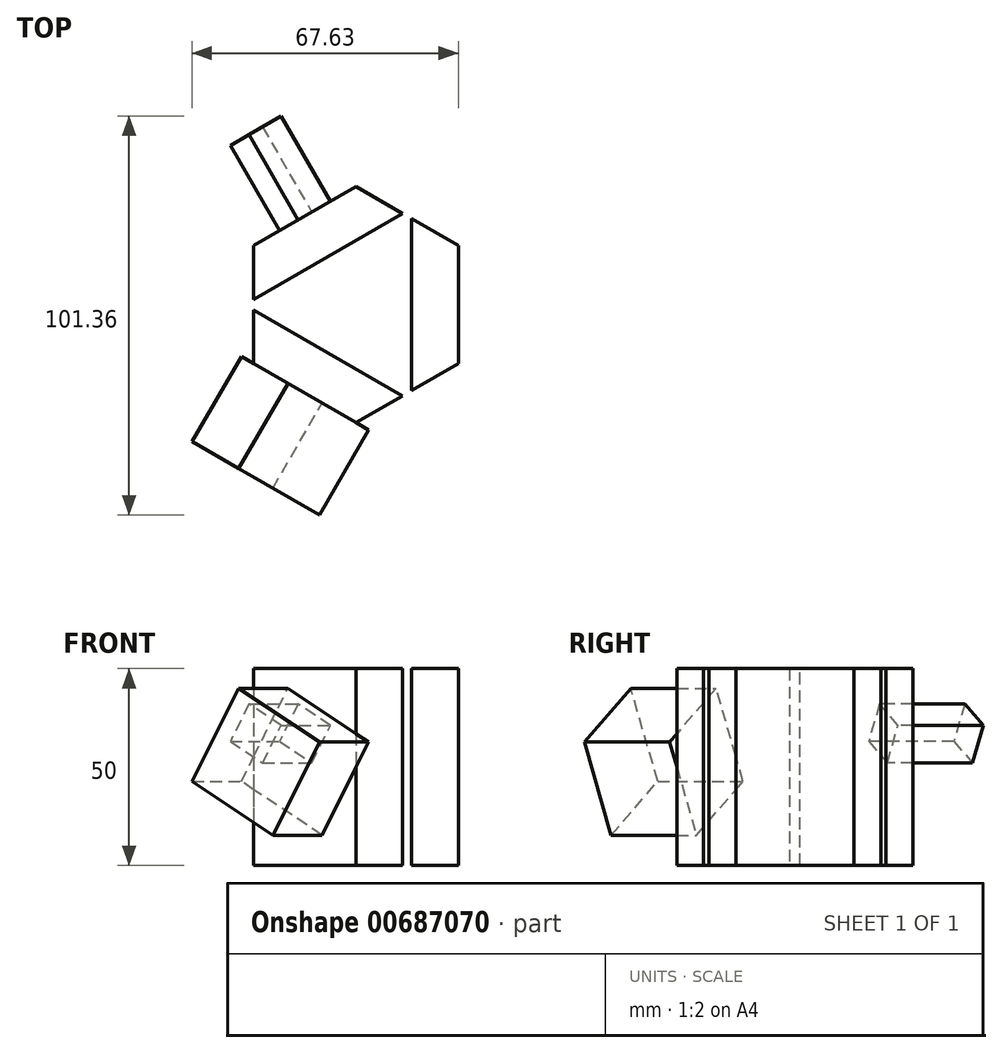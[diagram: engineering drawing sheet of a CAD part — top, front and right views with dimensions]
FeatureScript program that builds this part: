
annotation { "Feature Type Name" : "Feature", "Feature Type Description" : "" }
export const myFeature = defineFeature(function(context is Context, id is Id, definition is map)
    precondition{}
    {
        {
            var Q0;
            Q0=qCreatedBy(makeId("Top.planeOp"),FACE);
            var sketch = newSketch(context, id + "F0", { "sketchPlane" : qUnion([Q0])});
            skCircle(sketch, "E0.cCircle", {"center": v(0, 0) * mm, "radius": 25.98 * mm, "construction": true});
            skLineSegment(sketch, "E0.0", {"start": v(-25.98, -15) * mm, "end": v(-25.98, 15) * mm});
            skLineSegment(sketch, "E0.1", {"start": v(-25.98, 15) * mm, "end": v(0, 30) * mm});
            skLineSegment(sketch, "E0.2", {"start": v(0, 30) * mm, "end": v(25.98, 15) * mm});
            skLineSegment(sketch, "E0.3", {"start": v(25.98, 15) * mm, "end": v(25.98, -15) * mm});
            skLineSegment(sketch, "E0.4", {"start": v(25.98, -15) * mm, "end": v(0, -30) * mm});
            skLineSegment(sketch, "E0.5", {"start": v(0, -30) * mm, "end": v(-25.98, -15) * mm});
            skPoint(sketch, "E0.0.midPoint", {"position": v(-25.98, 0) * mm});
            skSolve(sketch);
        }
        {
            var Q0;
            Q0 = qSketchRegion(id + "F0", true);
            extrude(context, id + "F1", {"entities" : qUnion([Q0]), "depth" : 50 * mm, "offsetDistance" : 25 * mm});
        }
        {
            var Q0;
            Q0=makeQuery(id+"F1.opExtrude","CAP_FACE",FACE,{"disambiguationData":[OSD([sQuery(id+"F0.wireOp",EDGE,"E0.0"),sQuery(id+"F0.wireOp",EDGE,"E0.1"),sQuery(id+"F0.wireOp",EDGE,"E0.2"),sQuery(id+"F0.wireOp",EDGE,"E0.3"),sQuery(id+"F0.wireOp",EDGE,"E0.4"),sQuery(id+"F0.wireOp",EDGE,"E0.5")])],"isStart":false});
            var sketch = newSketch(context, id + "F2", { "sketchPlane" : qUnion([Q0])});
            skCircle(sketch, "E1.cCircle", {"center": v(0, 0) * mm, "radius": 14.15 * mm, "construction": true});
            skLineSegment(sketch, "E1.0", {"start": v(-28.3, 0) * mm, "end": v(14.15, 24.5) * mm});
            skLineSegment(sketch, "E1.1", {"start": v(14.15, 24.5) * mm, "end": v(14.15, -24.5) * mm});
            skLineSegment(sketch, "E1.2", {"start": v(14.15, -24.5) * mm, "end": v(-28.3, 0) * mm});
            skPoint(sketch, "E1.0.midPoint", {"position": v(-7.07, 12.25) * mm});
            skSolve(sketch);
        }
        {
            var Q0;
            Q0 = qSketchRegion(id + "F2", true);
            extrude(context, id + "F3", {"entities" : qUnion([Q0]), "operationType" : NewBodyOperationType.REMOVE, "oppositeDirection" : true, "depth" : 50 * mm, "offsetDistance" : 25 * mm});
        }
        {
            var Q0;
            Q0=makeQuery(id+"F1.opExtrude","SWEPT_FACE",FACE,{"disambiguationData":[OSD([sQuery(id+"F0.wireOp",EDGE,"E0.5")])]});
            var sketch = newSketch(context, id + "F4", { "sketchPlane" : qUnion([Q0])});
            skCircle(sketch, "E2.cCircle", {"center": v(0, 26.34) * mm, "radius": 13.66 * mm, "construction": true});
            skLineSegment(sketch, "E2.0", {"start": v(-18.66, 21.34) * mm, "end": v(-5, 45) * mm});
            skLineSegment(sketch, "E2.1", {"start": v(-5, 45) * mm, "end": v(18.66, 31.34) * mm});
            skLineSegment(sketch, "E2.2", {"start": v(18.66, 31.34) * mm, "end": v(5, 7.68) * mm});
            skLineSegment(sketch, "E2.3", {"start": v(5, 7.68) * mm, "end": v(-18.66, 21.34) * mm});
            skPoint(sketch, "E2.0.midPoint", {"position": v(-11.83, 33.17) * mm});
            skSolve(sketch);
        }
        {
            var Q0;
            Q0 = qSketchRegion(id + "F4", true);
            extrude(context, id + "F5", {"entities" : qUnion([Q0]), "operationType" : NewBodyOperationType.ADD, "depth" : 25 * mm, "offsetDistance" : 25 * mm});
        }
        {
            var Q0;
            Q0=makeQuery(id+"F1.opExtrude","SWEPT_FACE",FACE,{"disambiguationData":[OSD([sQuery(id+"F0.wireOp",EDGE,"E0.1")])]});
            var sketch = newSketch(context, id + "F6", { "sketchPlane" : qUnion([Q0])});
            skCircle(sketch, "E3.cCircle", {"center": v(0, 33.54) * mm, "radius": 5.46 * mm, "construction": true});
            skLineSegment(sketch, "E3.0", {"start": v(7.46, 31.54) * mm, "end": v(-2, 26.07) * mm});
            skLineSegment(sketch, "E3.1", {"start": v(-2, 26.07) * mm, "end": v(-7.46, 35.54) * mm});
            skLineSegment(sketch, "E3.2", {"start": v(-7.46, 35.54) * mm, "end": v(2, 41) * mm});
            skLineSegment(sketch, "E3.3", {"start": v(2, 41) * mm, "end": v(7.46, 31.54) * mm});
            skPoint(sketch, "E3.0.midPoint", {"position": v(2.73, 28.8) * mm});
            skSolve(sketch);
        }
        {
            var Q0;
            Q0 = qSketchRegion(id + "F6", true);
            extrude(context, id + "F7", {"entities" : qUnion([Q0]), "operationType" : NewBodyOperationType.ADD, "depth" : 25 * mm, "offsetDistance" : 25 * mm});
        }
    });
